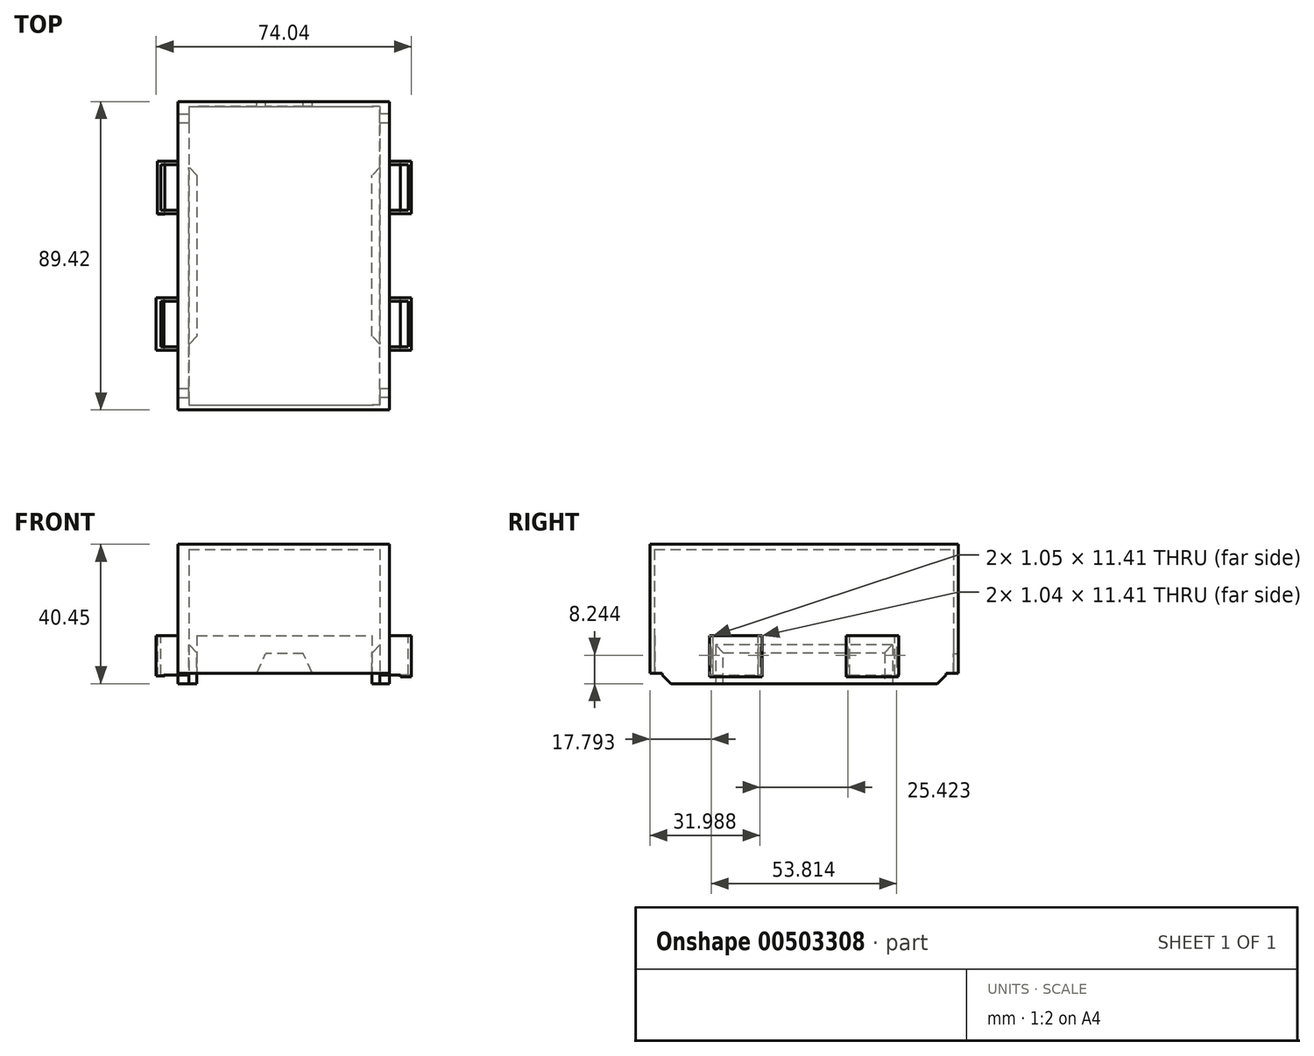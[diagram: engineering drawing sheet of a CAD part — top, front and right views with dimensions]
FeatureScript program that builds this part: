
annotation { "Feature Type Name" : "Feature", "Feature Type Description" : "" }
export const myFeature = defineFeature(function(context is Context, id is Id, definition is map)
    precondition{}
    {
        {
            var Q0;
            Q0=qCreatedBy(makeId("Top.planeOp"),FACE);
            var sketch = newSketch(context, id + "F0", { "sketchPlane" : qUnion([Q0])});
            skLineSegment(sketch, "E0.bottom", {"start": v(-30.48, 45.72) * mm, "end": v(30.48, 45.72) * mm});
            skLineSegment(sketch, "E0.top", {"start": v(-30.48, -45.72) * mm, "end": v(30.48, -45.72) * mm});
            skLineSegment(sketch, "E0.left", {"start": v(-30.48, 45.72) * mm, "end": v(-30.48, -45.72) * mm});
            skLineSegment(sketch, "E0.right", {"start": v(30.48, 45.72) * mm, "end": v(30.48, -45.72) * mm});
            skPoint(sketch, "E0.middle", {"position": v(0, 0) * mm});
            skLineSegment(sketch, "E1.bottom", {"start": v(-25.4, 43.3) * mm, "end": v(25.4, 43.3) * mm});
            skLineSegment(sketch, "E1.top", {"start": v(-25.4, -43.3) * mm, "end": v(25.4, -43.3) * mm});
            skLineSegment(sketch, "E1.left", {"start": v(-25.4, 43.3) * mm, "end": v(-25.4, -43.3) * mm});
            skLineSegment(sketch, "E1.right", {"start": v(25.4, 43.3) * mm, "end": v(25.4, -43.3) * mm});
            skSolve(sketch);
        }
        {
            var Q0;
            Q0=makeQuery(id+"F0.imprint","IMPRINT",FACE,{"disambiguationData":[TD([[makeQuery(id+"F0.imprint","IMPRINT",EDGE,{"derivedFrom":sQuery(id+"F0.wireOp",EDGE,"E0.bottom")}),-1.0]])]});
            extrude(context, id + "F1", {"entities" : qUnion([Q0]), "depth" : 28.45 * mm});
        }
        {
            var Q0;
            Q0=makeQuery(id+"F1.opExtrude","SWEPT_FACE",FACE,{"disambiguationData":[OSD([sQuery(id+"F0.wireOp",EDGE,"E0.bottom")])]});
            var sketch = newSketch(context, id + "F2", { "sketchPlane" : qUnion([Q0])});
            skLineSegment(sketch, "E2", {"start": v(30.48, 14.22) * mm, "end": v(-30.48, 14.22) * mm, "construction": true});
            skPoint(sketch, "E3.middle", {"position": v(0, 28.45) * mm});
            skLineSegment(sketch, "E4", {"start": v(0, 0) * mm, "end": v(-9.48, 0) * mm});
            skLineSegment(sketch, "E5.bottom", {"start": v(-5.46, 19.69) * mm, "end": v(5.46, 19.69) * mm});
            skLineSegment(sketch, "E5.top", {"start": v(-5.46, 8.76) * mm, "end": v(5.46, 8.76) * mm});
            skPoint(sketch, "E5.middle", {"position": v(0, 14.22) * mm});
            skLineSegment(sketch, "E6", {"start": v(-9.48, 0) * mm, "end": v(-5.46, 8.76) * mm});
            skLineSegment(sketch, "E7.MirrorCS", {"start": v(0, 0) * mm, "end": v(9.48, 0) * mm});
            skLineSegment(sketch, "E8.MirrorCS", {"start": v(9.48, 0) * mm, "end": v(5.46, 8.76) * mm});
            skLineSegment(sketch, "E9.MirrorCS", {"start": v(-5.46, 19.68) * mm, "end": v(5.46, 19.68) * mm});
            skLineSegment(sketch, "E10.MirrorCS", {"start": v(-9.48, 28.45) * mm, "end": v(-5.46, 19.68) * mm});
            skLineSegment(sketch, "E11.MirrorCS", {"start": v(0, 28.45) * mm, "end": v(-9.48, 28.45) * mm});
            skLineSegment(sketch, "E12.MirrorCS", {"start": v(0, 28.45) * mm, "end": v(9.48, 28.45) * mm});
            skLineSegment(sketch, "E13.MirrorCS", {"start": v(9.48, 28.45) * mm, "end": v(5.46, 19.68) * mm});
            skSolve(sketch);
        }
        {
            var Q0;
            Q0=qSketchRegion(id+"F2",true);
            var Q1;
            {var subQ1=sQuery(id+"F2.wireOp",EDGE,"z2dX2tQm-mAHQ-A0xj-hADe-n06FKAJlfdiZ.bottom");Q1=makeQuery(id+"F2.imprint","IMPRINT",FACE,{"disambiguationData":[TD([[makeQuery(id+"F2.imprint","IMPRINT",EDGE,{"derivedFrom":subQ1}),-1.0]])]});}
            extrude(context, id + "F3", {"entities" : qUnion([Q0, Q1]), "operationType" : NewBodyOperationType.REMOVE, "oppositeDirection" : true, "depth" : 25.4 * mm});
        }
        {
            var Q0;
            Q0=qCreatedBy(makeId("Top.planeOp"),FACE);
            var sketch = newSketch(context, id + "F4", { "sketchPlane" : qUnion([Q0])});
            skLineSegment(sketch, "E14.bottom", {"start": v(33.22, 48.14) * mm, "end": v(-33.43, 48.14) * mm});
            skLineSegment(sketch, "E14.top", {"start": v(33.22, 41.15) * mm, "end": v(-33.43, 41.15) * mm});
            skLineSegment(sketch, "E14.left", {"start": v(33.22, 48.14) * mm, "end": v(33.22, 41.15) * mm});
            skLineSegment(sketch, "E14.right", {"start": v(-33.43, 48.14) * mm, "end": v(-33.43, 41.15) * mm});
            skLineSegment(sketch, "E15.MirrorCS", {"start": v(33.22, -41.15) * mm, "end": v(-33.43, -41.15) * mm});
            skLineSegment(sketch, "E16.MirrorCS", {"start": v(33.22, -48.14) * mm, "end": v(33.22, -41.15) * mm});
            skLineSegment(sketch, "E17.MirrorCS", {"start": v(-33.43, -48.14) * mm, "end": v(-33.43, -41.15) * mm});
            skLineSegment(sketch, "E18.MirrorCS", {"start": v(33.22, -48.14) * mm, "end": v(-33.43, -48.14) * mm});
            skSolve(sketch);
        }
        {
            var Q0;
            Q0=qSketchRegion(id+"F4",true);
            extrude(context, id + "F5", {"entities" : qUnion([Q0]), "operationType" : NewBodyOperationType.REMOVE, "depth" : 3.05 * mm});
        }
        {
            var Q0;
            Q0=makeQuery(id+"F1.opExtrude","CAP_FACE",FACE,{"disambiguationData":[OSD([sQuery(id+"F0.wireOp",EDGE,"E0.bottom"),sQuery(id+"F0.wireOp",EDGE,"E0.top"),sQuery(id+"F0.wireOp",EDGE,"E0.left"),sQuery(id+"F0.wireOp",EDGE,"E0.right"),sQuery(id+"F0.wireOp",EDGE,"E1.bottom"),sQuery(id+"F0.wireOp",EDGE,"E1.top"),sQuery(id+"F0.wireOp",EDGE,"E1.left"),sQuery(id+"F0.wireOp",EDGE,"E1.right")])],"isStart":false});
            var sketch = newSketch(context, id + "F6", { "sketchPlane" : qUnion([Q0])});
            skLineSegment(sketch, "E19.bottom", {"start": v(30.48, 45.72) * mm, "end": v(-34.49, 45.72) * mm});
            skLineSegment(sketch, "E19.top", {"start": v(30.48, 40.94) * mm, "end": v(-34.49, 40.94) * mm});
            skLineSegment(sketch, "E19.left", {"start": v(30.48, 45.72) * mm, "end": v(30.48, 40.94) * mm});
            skLineSegment(sketch, "E19.right", {"start": v(-34.49, 45.72) * mm, "end": v(-34.49, 40.94) * mm});
            skLineSegment(sketch, "E20.MirrorCS", {"start": v(30.48, -40.94) * mm, "end": v(-34.49, -40.94) * mm});
            skLineSegment(sketch, "E21.MirrorCS", {"start": v(30.48, -45.72) * mm, "end": v(30.48, -40.94) * mm});
            skLineSegment(sketch, "E22.MirrorCS", {"start": v(-34.49, -45.72) * mm, "end": v(-34.49, -40.94) * mm});
            skLineSegment(sketch, "E23.MirrorCS", {"start": v(30.48, -45.72) * mm, "end": v(-34.49, -45.72) * mm});
            skSolve(sketch);
        }
        {
            var Q0;
            Q0=qSketchRegion(id+"F6",true);
            extrude(context, id + "F7", {"entities" : qUnion([Q0]), "operationType" : NewBodyOperationType.REMOVE, "oppositeDirection" : true, "depth" : 3.05 * mm});
        }
        {
            var Q0;
            Q0=makeQuery(id+"F1.opExtrude","SWEPT_FACE",FACE,{"disambiguationData":[OSD([sQuery(id+"F0.wireOp",EDGE,"E1.right")])]});
            var sketch = newSketch(context, id + "F8", { "sketchPlane" : qUnion([Q0])});
            skLineSegment(sketch, "E24.bottom", {"start": v(-41.15, 0) * mm, "end": v(-25.91, 0) * mm});
            skLineSegment(sketch, "E24.top", {"start": v(-41.15, 30.48) * mm, "end": v(-25.91, 30.48) * mm});
            skLineSegment(sketch, "E24.right", {"start": v(-25.91, 0) * mm, "end": v(-25.91, 30.48) * mm});
            skLineSegment(sketch, "E25", {"start": v(0, 0) * mm, "end": v(0, 28.45) * mm, "construction": true});
            skLineSegment(sketch, "E26.MirrorCS", {"start": v(25.91, 0) * mm, "end": v(25.91, 30.48) * mm});
            skLineSegment(sketch, "E27.MirrorCS", {"start": v(41.15, 30.48) * mm, "end": v(25.91, 30.48) * mm});
            skLineSegment(sketch, "E28.MirrorCS", {"start": v(41.15, 0) * mm, "end": v(25.91, 0) * mm});
            skLineSegment(sketch, "E29", {"start": v(-41.15, 30.48) * mm, "end": v(-43.09, 30.48) * mm});
            skLineSegment(sketch, "E30", {"start": v(-43.09, 30.48) * mm, "end": v(-43.09, 0) * mm});
            skLineSegment(sketch, "E31", {"start": v(-43.09, 0) * mm, "end": v(-41.15, 0) * mm});
            skLineSegment(sketch, "E32.MirrorCS", {"start": v(41.15, 30.48) * mm, "end": v(43.09, 30.48) * mm});
            skLineSegment(sketch, "E33.MirrorCS", {"start": v(43.09, 30.48) * mm, "end": v(43.09, 0) * mm});
            skLineSegment(sketch, "E34.MirrorCS", {"start": v(43.09, 0) * mm, "end": v(41.15, 0) * mm});
            skSolve(sketch);
        }
        {
            var Q0;
            Q0=qSketchRegion(id+"F8",true);
            extrude(context, id + "F9", {"entities" : qUnion([Q0]), "operationType" : NewBodyOperationType.REMOVE, "oppositeDirection" : true, "depth" : 2.3 * mm});
        }
        {
            var Q0;
            Q0=qCreatedBy(makeId("Right.planeOp"),FACE);
            var sketch = newSketch(context, id + "F10", { "sketchPlane" : qUnion([Q0])});
            skLineSegment(sketch, "E35.bottom", {"start": v(51.68, -10.67) * mm, "end": v(-48.17, -10.67) * mm});
            skLineSegment(sketch, "E35.top", {"start": v(51.68, 37.54) * mm, "end": v(-48.17, 37.54) * mm});
            skLineSegment(sketch, "E35.left", {"start": v(51.68, -10.67) * mm, "end": v(51.68, 37.54) * mm});
            skLineSegment(sketch, "E35.right", {"start": v(-48.17, -10.67) * mm, "end": v(-48.17, 37.54) * mm});
            skSolve(sketch);
        }
        {
            var Q0;
            Q0=qSketchRegion(id+"F10",true);
            extrude(context, id + "F11", {"entities" : qUnion([Q0]), "operationType" : NewBodyOperationType.REMOVE, "oppositeDirection" : true, "depth" : 50.8 * mm});
        }
        {
            var Q0;
            Q0=makeQuery(id+"F1.opExtrude","SWEPT_BODY",BODY,{"disambiguationData":[OSD([sQuery(id+"F0.wireOp",EDGE,"E0.bottom"),sQuery(id+"F0.wireOp",EDGE,"E0.top"),sQuery(id+"F0.wireOp",EDGE,"E0.left"),sQuery(id+"F0.wireOp",EDGE,"E0.right"),sQuery(id+"F0.wireOp",EDGE,"E1.bottom"),sQuery(id+"F0.wireOp",EDGE,"E1.top"),sQuery(id+"F0.wireOp",EDGE,"E1.left"),sQuery(id+"F0.wireOp",EDGE,"E1.right")])]});
            var Q1;
            Q1=qCreatedBy(makeId("Right.planeOp"),FACE);
            mirror(context, id + "F12", {"operationType" : NewBodyOperationType.ADD, "entities" : qUnion([Q0]), "mirrorPlane" : qUnion([Q1])});
        }
        {
            var Q0;
            {var subQ1=sQuery(id+"F0.wireOp",EDGE,"E0.right");var subQ2=sQuery(id+"F6.wireOp",EDGE,"E19.top");Q0=makeQuery(id+"F12.opPattern","COPY",EDGE,{"derivedFrom":makeQuery(id+"F7.boolean.opBoolean","COPY",EDGE,{"disambiguationData":[TD([makeQuery(id+"F1.opExtrude","SWEPT_FACE",FACE,{"disambiguationData":[OSD([subQ1])]})])],"derivedFrom":makeQuery(id+"F7.opExtrude","CAP_EDGE",EDGE,{"disambiguationData":[OSD([subQ2])],"isStart":true})}),"instanceName":"1"});}
            var Q1;
            {var subQ1=sQuery(id+"F0.wireOp",EDGE,"E0.right");var subQ2=sQuery(id+"F4.wireOp",EDGE,"E14.top");Q1=makeQuery(id+"F12.opPattern","COPY",EDGE,{"derivedFrom":makeQuery(id+"F5.boolean.opBoolean","COPY",EDGE,{"disambiguationData":[TD([makeQuery(id+"F1.opExtrude","SWEPT_FACE",FACE,{"disambiguationData":[OSD([subQ1])]})])],"derivedFrom":makeQuery(id+"F5.opExtrude","CAP_EDGE",EDGE,{"disambiguationData":[OSD([subQ2])],"isStart":true})}),"instanceName":"1"});}
            var Q2;
            {var subQ1=sQuery(id+"F0.wireOp",EDGE,"E0.right");var subQ2=sQuery(id+"F6.wireOp",EDGE,"E19.top");Q2=makeQuery(id+"F7.boolean.opBoolean","COPY",EDGE,{"disambiguationData":[TD([makeQuery(id+"F1.opExtrude","SWEPT_FACE",FACE,{"disambiguationData":[OSD([subQ1])]})])],"derivedFrom":makeQuery(id+"F7.opExtrude","CAP_EDGE",EDGE,{"disambiguationData":[OSD([subQ2])],"isStart":true})});}
            var Q3;
            {var subQ1=sQuery(id+"F0.wireOp",EDGE,"E0.right");var subQ2=sQuery(id+"F6.wireOp",EDGE,"E20.MirrorCS");Q3=makeQuery(id+"F7.boolean.opBoolean","COPY",EDGE,{"disambiguationData":[TD([makeQuery(id+"F1.opExtrude","SWEPT_FACE",FACE,{"disambiguationData":[OSD([subQ1])]})])],"derivedFrom":makeQuery(id+"F7.opExtrude","CAP_EDGE",EDGE,{"disambiguationData":[OSD([subQ2])],"isStart":true})});}
            var Q4;
            {var subQ1=sQuery(id+"F0.wireOp",EDGE,"E0.right");var subQ2=sQuery(id+"F6.wireOp",EDGE,"E20.MirrorCS");Q4=makeQuery(id+"F12.opPattern","COPY",EDGE,{"derivedFrom":makeQuery(id+"F7.boolean.opBoolean","COPY",EDGE,{"disambiguationData":[TD([makeQuery(id+"F1.opExtrude","SWEPT_FACE",FACE,{"disambiguationData":[OSD([subQ1])]})])],"derivedFrom":makeQuery(id+"F7.opExtrude","CAP_EDGE",EDGE,{"disambiguationData":[OSD([subQ2])],"isStart":true})}),"instanceName":"1"});}
            var Q5;
            {var subQ1=sQuery(id+"F0.wireOp",EDGE,"E0.right");var subQ2=sQuery(id+"F4.wireOp",EDGE,"E15.MirrorCS");Q5=makeQuery(id+"F12.opPattern","COPY",EDGE,{"derivedFrom":makeQuery(id+"F5.boolean.opBoolean","COPY",EDGE,{"disambiguationData":[TD([makeQuery(id+"F1.opExtrude","SWEPT_FACE",FACE,{"disambiguationData":[OSD([subQ1])]})])],"derivedFrom":makeQuery(id+"F5.opExtrude","CAP_EDGE",EDGE,{"disambiguationData":[OSD([subQ2])],"isStart":true})}),"instanceName":"1"});}
            var Q6;
            {var subQ1=sQuery(id+"F0.wireOp",EDGE,"E0.right");var subQ2=sQuery(id+"F4.wireOp",EDGE,"E15.MirrorCS");Q6=makeQuery(id+"F5.boolean.opBoolean","COPY",EDGE,{"disambiguationData":[TD([makeQuery(id+"F1.opExtrude","SWEPT_FACE",FACE,{"disambiguationData":[OSD([subQ1])]})])],"derivedFrom":makeQuery(id+"F5.opExtrude","CAP_EDGE",EDGE,{"disambiguationData":[OSD([subQ2])],"isStart":true})});}
            var Q7;
            {var subQ1=sQuery(id+"F0.wireOp",EDGE,"E0.right");var subQ2=sQuery(id+"F4.wireOp",EDGE,"E14.top");Q7=makeQuery(id+"F5.boolean.opBoolean","COPY",EDGE,{"disambiguationData":[TD([makeQuery(id+"F1.opExtrude","SWEPT_FACE",FACE,{"disambiguationData":[OSD([subQ1])]})])],"derivedFrom":makeQuery(id+"F5.opExtrude","CAP_EDGE",EDGE,{"disambiguationData":[OSD([subQ2])],"isStart":true})});}
            var Q8;
            Q8=makeQuery(id+"F9.boolean.opBoolean","COPY",EDGE,{"derivedFrom":makeQuery(id+"F9.opExtrude","CAP_EDGE",EDGE,{"disambiguationData":[OSD([sQuery(id+"F8.wireOp",EDGE,"E24.right")])],"isStart":true})});
            var Q9;
            Q9=makeQuery(id+"F9.boolean.opBoolean","COPY",EDGE,{"derivedFrom":makeQuery(id+"F9.opExtrude","CAP_EDGE",EDGE,{"disambiguationData":[OSD([sQuery(id+"F8.wireOp",EDGE,"E26.MirrorCS")])],"isStart":true})});
            var Q10;
            Q10=makeQuery(id+"F12.opPattern","COPY",EDGE,{"derivedFrom":makeQuery(id+"F9.boolean.opBoolean","COPY",EDGE,{"derivedFrom":makeQuery(id+"F9.opExtrude","CAP_EDGE",EDGE,{"disambiguationData":[OSD([sQuery(id+"F8.wireOp",EDGE,"E24.right")])],"isStart":true})}),"instanceName":"1"});
            var Q11;
            Q11=makeQuery(id+"F12.opPattern","COPY",EDGE,{"derivedFrom":makeQuery(id+"F9.boolean.opBoolean","COPY",EDGE,{"derivedFrom":makeQuery(id+"F9.opExtrude","CAP_EDGE",EDGE,{"disambiguationData":[OSD([sQuery(id+"F8.wireOp",EDGE,"E26.MirrorCS")])],"isStart":true})}),"instanceName":"1"});
            chamfer(context, id + "F13", {"entities" : qUnion([Q0, Q1, Q2, Q3, Q4, Q5, Q6, Q7, Q8, Q9, Q10, Q11]), "width" : 2.54 * mm, "tangentPropagation" : true});
        }
        {
            var Q0;
            Q0=makeQuery(id+"F1.opExtrude","SWEPT_FACE",FACE,{"disambiguationData":[OSD([sQuery(id+"F0.wireOp",EDGE,"E0.right")])]});
            var sketch = newSketch(context, id + "F14", { "sketchPlane" : qUnion([Q0])});
            skLineSegment(sketch, "E36.bottom", {"start": v(-27.43, 25.9) * mm, "end": v(-12.2, 25.9) * mm});
            skLineSegment(sketch, "E36.top", {"start": v(-27.43, 2.54) * mm, "end": v(-12.2, 2.54) * mm});
            skLineSegment(sketch, "E36.left", {"start": v(-27.43, 25.9) * mm, "end": v(-27.43, 2.54) * mm});
            skLineSegment(sketch, "E36.right", {"start": v(-12.2, 25.9) * mm, "end": v(-12.2, 2.54) * mm});
            skLineSegment(sketch, "E37.MirrorCS", {"start": v(12.2, 25.9) * mm, "end": v(12.2, 2.54) * mm});
            skLineSegment(sketch, "E38.MirrorCS", {"start": v(27.43, 25.9) * mm, "end": v(12.2, 25.9) * mm});
            skLineSegment(sketch, "E39.MirrorCS", {"start": v(27.43, 2.54) * mm, "end": v(12.2, 2.54) * mm});
            skLineSegment(sketch, "E40.MirrorCS", {"start": v(27.43, 25.9) * mm, "end": v(27.43, 2.54) * mm});
            skSolve(sketch);
        }
        {
            var Q0;
            Q0=qSketchRegion(id+"F14",true);
            extrude(context, id + "F15", {"entities" : qUnion([Q0]), "operationType" : NewBodyOperationType.ADD, "depth" : 6.35 * mm});
        }
        {
            var Q0;
            Q0=makeQuery(id+"F15.opExtrude","SWEPT_FACE",FACE,{"disambiguationData":[OSD([sQuery(id+"F14.wireOp",EDGE,"E36.bottom")])]});
            var sketch = newSketch(context, id + "F16", { "sketchPlane" : qUnion([Q0])});
            skLineSegment(sketch, "E41.bottom", {"start": v(30.48, -26.38) * mm, "end": v(35.84, -26.38) * mm});
            skLineSegment(sketch, "E41.top", {"start": v(30.48, -13.23) * mm, "end": v(35.84, -13.23) * mm});
            skLineSegment(sketch, "E41.left", {"start": v(30.48, -26.38) * mm, "end": v(30.48, -13.23) * mm});
            skLineSegment(sketch, "E41.right", {"start": v(35.84, -26.38) * mm, "end": v(35.84, -13.23) * mm});
            skLineSegment(sketch, "E42.MirrorCS", {"start": v(30.48, 13.23) * mm, "end": v(35.84, 13.23) * mm});
            skLineSegment(sketch, "E43.MirrorCS", {"start": v(35.84, 26.38) * mm, "end": v(35.84, 13.23) * mm});
            skLineSegment(sketch, "E44.MirrorCS", {"start": v(30.48, 26.38) * mm, "end": v(35.84, 26.38) * mm});
            skLineSegment(sketch, "E45.MirrorCS", {"start": v(30.48, 26.38) * mm, "end": v(30.48, 13.23) * mm});
            skSolve(sketch);
        }
        {
            var Q0;
            Q0=qSketchRegion(id+"F16",true);
            extrude(context, id + "F17", {"entities" : qUnion([Q0]), "operationType" : NewBodyOperationType.REMOVE, "endBound" : BoundingType.THROUGH_ALL, "oppositeDirection" : true, "depth" : 25.4 * mm});
        }
        {
            var Q0;
            Q0=makeQuery(id+"F1.opExtrude","SWEPT_BODY",BODY,{"disambiguationData":[OSD([sQuery(id+"F0.wireOp",EDGE,"E0.bottom"),sQuery(id+"F0.wireOp",EDGE,"E0.top"),sQuery(id+"F0.wireOp",EDGE,"E0.left"),sQuery(id+"F0.wireOp",EDGE,"E0.right"),sQuery(id+"F0.wireOp",EDGE,"E1.bottom"),sQuery(id+"F0.wireOp",EDGE,"E1.top"),sQuery(id+"F0.wireOp",EDGE,"E1.left"),sQuery(id+"F0.wireOp",EDGE,"E1.right")])]});
            var Q1;
            Q1=qCreatedBy(makeId("Right.planeOp"),FACE);
            mirror(context, id + "F18", {"operationType" : NewBodyOperationType.ADD, "entities" : qUnion([Q0]), "mirrorPlane" : qUnion([Q1])});
        }
        {
            var Q0;
            Q0=makeQuery(id+"F9.boolean.opBoolean","COPY",FACE,{"derivedFrom":makeQuery(id+"F9.opExtrude","SWEPT_FACE",FACE,{"disambiguationData":[OSD([sQuery(id+"F8.wireOp",EDGE,"E33.MirrorCS")])]})});
            var Q1;
            Q1=makeQuery(id+"F12.opPattern","COPY",FACE,{"derivedFrom":makeQuery(id+"F9.boolean.opBoolean","COPY",FACE,{"derivedFrom":makeQuery(id+"F9.opExtrude","SWEPT_FACE",FACE,{"disambiguationData":[OSD([sQuery(id+"F8.wireOp",EDGE,"E33.MirrorCS")])]})}),"instanceName":"1"});
            extrude(context, id + "F19", {"entities" : qUnion([Q0, Q1]), "operationType" : NewBodyOperationType.REMOVE, "oppositeDirection" : true, "depth" : 0.25 * mm});
        }
        {
            var Q0;
            Q0=makeQuery(id+"F9.boolean.opBoolean","COPY",FACE,{"derivedFrom":makeQuery(id+"F9.opExtrude","SWEPT_FACE",FACE,{"disambiguationData":[OSD([sQuery(id+"F8.wireOp",EDGE,"E30")])]})});
            var Q1;
            Q1=makeQuery(id+"F12.opPattern","COPY",FACE,{"derivedFrom":makeQuery(id+"F9.boolean.opBoolean","COPY",FACE,{"derivedFrom":makeQuery(id+"F9.opExtrude","SWEPT_FACE",FACE,{"disambiguationData":[OSD([sQuery(id+"F8.wireOp",EDGE,"E30")])]})}),"instanceName":"1"});
            extrude(context, id + "F20", {"entities" : qUnion([Q0, Q1]), "operationType" : NewBodyOperationType.REMOVE, "oppositeDirection" : true, "depth" : 0.25 * mm});
        }
        {
            var Q0;
            {var subQ0=makeQuery(id+"F1.opExtrude","SWEPT_FACE",FACE,{"disambiguationData":[OSD([sQuery(id+"F0.wireOp",EDGE,"E0.top")])]});Q0=makeQuery(id+"F12.boolean.opBoolean","MERGE",FACE,{"derivedFrom":[subQ0,makeQuery(id+"F12.opPattern","COPY",FACE,{"derivedFrom":subQ0,"instanceName":"1"})]});}
            extrude(context, id + "F21", {"entities" : qUnion([Q0]), "operationType" : NewBodyOperationType.REMOVE, "oppositeDirection" : true, "depth" : 1.02 * mm});
        }
        {
            var Q0;
            Q0=makeQuery(id+"F18.opPattern","COPY",FACE,{"derivedFrom":makeQuery(id+"F15.opExtrude","SWEPT_FACE",FACE,{"disambiguationData":[OSD([sQuery(id+"F14.wireOp",EDGE,"E38.MirrorCS")])]}),"instanceName":"1"});
            var sketch = newSketch(context, id + "F22", { "sketchPlane" : qUnion([Q0])});
            skLineSegment(sketch, "E46.bottom", {"start": v(-36.83, 27.43) * mm, "end": v(-33.66, 27.43) * mm});
            skLineSegment(sketch, "E46.top", {"start": v(-36.83, 12.2) * mm, "end": v(-33.66, 12.2) * mm});
            skLineSegment(sketch, "E46.left", {"start": v(-36.83, 27.43) * mm, "end": v(-36.83, 12.2) * mm});
            skLineSegment(sketch, "E46.right", {"start": v(-33.66, 27.43) * mm, "end": v(-33.66, 12.2) * mm});
            skLineSegment(sketch, "E47.bottom", {"start": v(-33.66, -12.01) * mm, "end": v(-36.83, -12.01) * mm});
            skLineSegment(sketch, "E47.top", {"start": v(-33.66, -27.44) * mm, "end": v(-36.83, -27.44) * mm});
            skLineSegment(sketch, "E47.left", {"start": v(-33.66, -12.01) * mm, "end": v(-33.66, -27.44) * mm});
            skLineSegment(sketch, "E47.right", {"start": v(-36.83, -12.01) * mm, "end": v(-36.83, -27.44) * mm});
            skSolve(sketch);
        }
        {
            var Q0;
            Q0=qSketchRegion(id+"F22",true);
            extrude(context, id + "F23", {"entities" : qUnion([Q0]), "operationType" : NewBodyOperationType.ADD, "depth" : 0.5 * mm});
        }
        {
            var Q0;
            Q0=makeQuery(id+"F15.opExtrude","SWEPT_FACE",FACE,{"disambiguationData":[OSD([sQuery(id+"F14.wireOp",EDGE,"E36.top")])]});
            var sketch = newSketch(context, id + "F24", { "sketchPlane" : qUnion([Q0])});
            skLineSegment(sketch, "E48.bottom", {"start": v(36.83, 27.43) * mm, "end": v(33.66, 27.43) * mm});
            skLineSegment(sketch, "E48.top", {"start": v(36.83, 12.2) * mm, "end": v(33.66, 12.2) * mm});
            skLineSegment(sketch, "E48.left", {"start": v(36.83, 27.43) * mm, "end": v(36.83, 12.2) * mm});
            skLineSegment(sketch, "E48.right", {"start": v(33.66, 27.43) * mm, "end": v(33.66, 12.2) * mm});
            skLineSegment(sketch, "E49.bottom", {"start": v(36.83, -12.2) * mm, "end": v(33.66, -12.2) * mm});
            skLineSegment(sketch, "E49.top", {"start": v(36.83, -27.38) * mm, "end": v(33.66, -27.38) * mm});
            skLineSegment(sketch, "E49.left", {"start": v(36.83, -12.2) * mm, "end": v(36.83, -27.38) * mm});
            skLineSegment(sketch, "E49.right", {"start": v(33.66, -12.2) * mm, "end": v(33.66, -27.38) * mm});
            skSolve(sketch);
        }
        {
            var Q0;
            Q0=qSketchRegion(id+"F24",true);
            extrude(context, id + "F25", {"entities" : qUnion([Q0]), "operationType" : NewBodyOperationType.ADD, "depth" : 0.5 * mm});
        }
        {
            var Q0;
            Q0=makeQuery(id+"F15.opExtrude","SWEPT_FACE",FACE,{"disambiguationData":[OSD([sQuery(id+"F14.wireOp",EDGE,"E36.bottom")])]});
            var sketch = newSketch(context, id + "F26", { "sketchPlane" : qUnion([Q0])});
            skLineSegment(sketch, "E50.bottom", {"start": v(36.83, -27.43) * mm, "end": v(35.34, -27.43) * mm});
            skLineSegment(sketch, "E50.top", {"start": v(36.83, -12.2) * mm, "end": v(35.34, -12.2) * mm});
            skLineSegment(sketch, "E50.left", {"start": v(36.83, -27.43) * mm, "end": v(36.83, -12.2) * mm});
            skLineSegment(sketch, "E50.right", {"start": v(35.34, -27.43) * mm, "end": v(35.34, -12.2) * mm});
            skLineSegment(sketch, "E51.bottom", {"start": v(35.34, 12.22) * mm, "end": v(36.83, 12.22) * mm});
            skLineSegment(sketch, "E51.top", {"start": v(35.34, 27.38) * mm, "end": v(36.83, 27.38) * mm});
            skLineSegment(sketch, "E51.left", {"start": v(35.34, 12.22) * mm, "end": v(35.34, 27.38) * mm});
            skLineSegment(sketch, "E51.right", {"start": v(36.83, 12.22) * mm, "end": v(36.83, 27.38) * mm});
            skSolve(sketch);
        }
        {
            var Q0;
            Q0=qSketchRegion(id+"F26",true);
            extrude(context, id + "F27", {"entities" : qUnion([Q0]), "operationType" : NewBodyOperationType.ADD, "depth" : 0.5 * mm});
        }
        {
            var Q0;
            Q0=makeQuery(id+"F18.opPattern","COPY",FACE,{"derivedFrom":makeQuery(id+"F15.opExtrude","SWEPT_FACE",FACE,{"disambiguationData":[OSD([sQuery(id+"F14.wireOp",EDGE,"E36.top")])]}),"instanceName":"1"});
            var sketch = newSketch(context, id + "F28", { "sketchPlane" : qUnion([Q0])});
            skLineSegment(sketch, "E52.bottom", {"start": v(-36.83, 12.2) * mm, "end": v(-35.32, 12.2) * mm});
            skLineSegment(sketch, "E52.top", {"start": v(-36.83, 27.43) * mm, "end": v(-35.32, 27.43) * mm});
            skLineSegment(sketch, "E52.left", {"start": v(-36.83, 12.2) * mm, "end": v(-36.83, 27.43) * mm});
            skLineSegment(sketch, "E52.right", {"start": v(-35.32, 12.2) * mm, "end": v(-35.32, 27.43) * mm});
            skLineSegment(sketch, "E53.bottom", {"start": v(-36.83, -12.06) * mm, "end": v(-35.34, -12.06) * mm});
            skLineSegment(sketch, "E53.top", {"start": v(-36.83, -27.45) * mm, "end": v(-35.34, -27.45) * mm});
            skLineSegment(sketch, "E53.left", {"start": v(-36.83, -12.06) * mm, "end": v(-36.83, -27.45) * mm});
            skLineSegment(sketch, "E53.right", {"start": v(-35.34, -12.06) * mm, "end": v(-35.34, -27.45) * mm});
            skSolve(sketch);
        }
        {
            var Q0;
            Q0=qSketchRegion(id+"F28",true);
            extrude(context, id + "F29", {"entities" : qUnion([Q0]), "operationType" : NewBodyOperationType.ADD, "depth" : 0.25 * mm});
        }
        {
            var Q0;
            Q0=makeQuery(id+"F12.opPattern","COPY",FACE,{"derivedFrom":makeQuery(id+"F1.opExtrude","SWEPT_FACE",FACE,{"disambiguationData":[OSD([sQuery(id+"F0.wireOp",EDGE,"E0.right")])]}),"instanceName":"1"});
            var Q1;
            Q1=makeQuery(id+"F29.opExtrude","SWEPT_FACE",FACE,{"disambiguationData":[OSD([sQuery(id+"F28.wireOp",EDGE,"E52.right")])]});
            var Q2;
            Q2=makeQuery(id+"F18.opPattern","COPY",FACE,{"derivedFrom":makeQuery(id+"F17.boolean.opBoolean","COPY",FACE,{"derivedFrom":makeQuery(id+"F17.opExtrude","SWEPT_FACE",FACE,{"disambiguationData":[OSD([sQuery(id+"F16.wireOp",EDGE,"E41.right")])]})}),"instanceName":"1"});
            var Q3;
            Q3=makeQuery(id+"F29.boolean.opBoolean","MERGE",FACE,{"derivedFrom":[makeQuery(id+"F23.boolean.opBoolean","MERGE",FACE,{"derivedFrom":[makeQuery(id+"F18.opPattern","COPY",FACE,{"derivedFrom":makeQuery(id+"F15.opExtrude","CAP_FACE",FACE,{"disambiguationData":[OSD([sQuery(id+"F14.wireOp",EDGE,"E36.bottom"),sQuery(id+"F14.wireOp",EDGE,"E36.top"),sQuery(id+"F14.wireOp",EDGE,"E36.left"),sQuery(id+"F14.wireOp",EDGE,"E36.right")])],"isStart":false}),"instanceName":"1"}),makeQuery(id+"F23.opExtrude","SWEPT_FACE",FACE,{"disambiguationData":[OSD([sQuery(id+"F22.wireOp",EDGE,"E47.right")])]})]}),makeQuery(id+"F29.opExtrude","SWEPT_FACE",FACE,{"disambiguationData":[OSD([sQuery(id+"F28.wireOp",EDGE,"E52.left")])]})]});
            extrude(context, id + "F30", {"entities" : qUnion([Q0, Q1, Q2, Q3]), "operationType" : NewBodyOperationType.ADD, "depth" : 0.38 * mm});
        }
        {
            var Q0;
            Q0=makeQuery(id+"F29.opExtrude","SWEPT_FACE",FACE,{"disambiguationData":[OSD([sQuery(id+"F28.wireOp",EDGE,"E53.right")])]});
            extrude(context, id + "F31", {"entities" : qUnion([Q0]), "operationType" : NewBodyOperationType.ADD, "depth" : 0.25 * mm});
        }
        {
            var Q0;
            {var subQ0=sQuery(id+"F0.wireOp",EDGE,"E0.right");var subQ1=sQuery(id+"F0.wireOp",EDGE,"E1.right");Q0=makeQuery(id+"F7.boolean.opBoolean","SPLIT",FACE,{"disambiguationData":[TD([makeQuery(id+"F1.opExtrude","SWEPT_FACE",FACE,{"disambiguationData":[OSD([subQ0])]})])],"derivedFrom":makeQuery(id+"F1.opExtrude","CAP_FACE",FACE,{"disambiguationData":[OSD([sQuery(id+"F0.wireOp",EDGE,"E0.bottom"),sQuery(id+"F0.wireOp",EDGE,"E0.top"),sQuery(id+"F0.wireOp",EDGE,"E0.left"),subQ0,sQuery(id+"F0.wireOp",EDGE,"E1.bottom"),sQuery(id+"F0.wireOp",EDGE,"E1.top"),sQuery(id+"F0.wireOp",EDGE,"E1.left"),subQ1])],"isStart":false})});}
            var sketch = newSketch(context, id + "F32", { "sketchPlane" : qUnion([Q0])});
            skLineSegment(sketch, "E54.bottom", {"start": v(64.06, -66.08) * mm, "end": v(-41.9, -66.08) * mm});
            skLineSegment(sketch, "E54.top", {"start": v(64.06, 50.2) * mm, "end": v(-41.9, 50.2) * mm});
            skLineSegment(sketch, "E54.left", {"start": v(64.06, -66.08) * mm, "end": v(64.06, 50.2) * mm});
            skLineSegment(sketch, "E54.right", {"start": v(-41.9, -66.08) * mm, "end": v(-41.9, 50.2) * mm});
            skSolve(sketch);
        }
        {
            var Q0;
            Q0 = qSketchRegion(id + "F32", true);
            extrude(context, id + "F33", {"entities" : qUnion([Q0]), "operationType" : NewBodyOperationType.REMOVE, "oppositeDirection" : true, "depth" : 14.5 * mm});
        }
        {
            var Q0;
            Q0=makeQuery(id+"F33.boolean.opBoolean","COPY",FACE,{"derivedFrom":makeQuery(id+"F33.opExtrude","CAP_FACE",FACE,{"disambiguationData":[OSD([sQuery(id+"F32.wireOp",EDGE,"E54.bottom"),sQuery(id+"F32.wireOp",EDGE,"E54.top"),sQuery(id+"F32.wireOp",EDGE,"E54.left"),sQuery(id+"F32.wireOp",EDGE,"E54.right")])],"isStart":false})});
            var sketch = newSketch(context, id + "F34", { "sketchPlane" : qUnion([Q0])});
            skLineSegment(sketch, "E55.bottom", {"start": v(-30.86, -44.7) * mm, "end": v(30.48, -44.7) * mm});
            skLineSegment(sketch, "E55.top", {"start": v(-30.86, 45.72) * mm, "end": v(30.48, 45.72) * mm});
            skLineSegment(sketch, "E55.left", {"start": v(-30.86, -44.7) * mm, "end": v(-30.86, 45.72) * mm});
            skLineSegment(sketch, "E55.right", {"start": v(30.48, -44.7) * mm, "end": v(30.48, 45.72) * mm});
            skLineSegment(sketch, "E56.bottom", {"start": v(-27.69, -43.34) * mm, "end": v(27.69, -43.34) * mm});
            skLineSegment(sketch, "E56.top", {"start": v(-27.69, 43.34) * mm, "end": v(27.69, 43.34) * mm});
            skLineSegment(sketch, "E56.left", {"start": v(-27.69, -43.34) * mm, "end": v(-27.69, 43.34) * mm});
            skLineSegment(sketch, "E56.right", {"start": v(27.69, -43.34) * mm, "end": v(27.69, 43.34) * mm});
            skSolve(sketch);
        }
        {
            var Q0;
            {var subQ27=sQuery(id+"F34.wireOp",EDGE,"E55.top");Q0=makeQuery(id+"F34.imprint","IMPRINT",FACE,{"disambiguationData":[TD([[makeQuery(id+"F34.imprint","IMPRINT",EDGE,{"derivedFrom":subQ27}),-1.0]])]});}
            extrude(context, id + "F35", {"entities" : qUnion([Q0]), "operationType" : NewBodyOperationType.ADD, "depth" : 25 * mm});
        }
        {
            var Q0;
            {var subQ0=sQuery(id+"F0.wireOp",EDGE,"E0.bottom");var subQ1=makeQuery(id+"F1.opExtrude","SWEPT_FACE",FACE,{"disambiguationData":[OSD([subQ0])]});Q0=makeQuery(id+"F35.boolean.opBoolean","MERGE",FACE,{"derivedFrom":[makeQuery(id+"F30.boolean.opBoolean","MERGE",FACE,{"derivedFrom":[makeQuery(id+"F12.boolean.opBoolean","MERGE",FACE,{"derivedFrom":[subQ1,makeQuery(id+"F12.opPattern","COPY",FACE,{"derivedFrom":subQ1,"instanceName":"1"})]}),makeQuery(id+"F30.opExtrude","SWEPT_FACE",FACE,{"disambiguationData":[OSD([subQ0,sQuery(id+"F0.wireOp",EDGE,"E0.right")])]})]}),makeQuery(id+"F35.opExtrude","SWEPT_FACE",FACE,{"disambiguationData":[OSD([sQuery(id+"F34.wireOp",EDGE,"E55.top")])]})]});}
            extrude(context, id + "F36", {"entities" : qUnion([Q0]), "operationType" : NewBodyOperationType.REMOVE, "oppositeDirection" : true, "depth" : 1 * mm});
        }
        {
            var Q0;
            Q0=makeQuery(id+"F31.opExtrude","CAP_FACE",FACE,{"disambiguationData":[OSD([sQuery(id+"F28.wireOp",EDGE,"E53.right")])],"isStart":false});
            extrude(context, id + "F37", {"entities" : qUnion([Q0]), "operationType" : NewBodyOperationType.ADD, "depth" : .4 * mm});
        }
        {
            var Q0;
            Q0=makeQuery(id+"F29.opExtrude","SWEPT_FACE",FACE,{"disambiguationData":[OSD([sQuery(id+"F28.wireOp",EDGE,"E52.right")])]});
            extrude(context, id + "F38", {"entities" : qUnion([Q0]), "operationType" : NewBodyOperationType.ADD, "depth" : .4 * mm});
        }
        {
            var Q0;
            Q0=makeQuery(id+"F35.opExtrude","CAP_FACE",FACE,{"disambiguationData":[OSD([sQuery(id+"F34.wireOp",EDGE,"E55.bottom"),sQuery(id+"F34.wireOp",EDGE,"E55.top"),sQuery(id+"F34.wireOp",EDGE,"E55.left"),sQuery(id+"F34.wireOp",EDGE,"E55.right"),sQuery(id+"F34.wireOp",EDGE,"E56.bottom"),sQuery(id+"F34.wireOp",EDGE,"E56.top"),sQuery(id+"F34.wireOp",EDGE,"E56.left"),sQuery(id+"F34.wireOp",EDGE,"E56.right")])],"isStart":false});
            var sketch = newSketch(context, id + "F39", { "sketchPlane" : qUnion([Q0])});
            skLineSegment(sketch, "E57.bottom", {"start": v(30.48, -44.7) * mm, "end": v(-30.86, -44.7) * mm});
            skLineSegment(sketch, "E57.top", {"start": v(30.48, 44.72) * mm, "end": v(-30.86, 44.72) * mm});
            skLineSegment(sketch, "E57.left", {"start": v(30.48, -44.7) * mm, "end": v(30.48, 44.72) * mm});
            skLineSegment(sketch, "E57.right", {"start": v(-30.86, -44.7) * mm, "end": v(-30.86, 44.72) * mm});
            skSolve(sketch);
        }
        {
            var Q0;
            Q0 = qSketchRegion(id + "F39", true);
            extrude(context, id + "F40", {"entities" : qUnion([Q0]), "operationType" : NewBodyOperationType.ADD, "depth" : 1.5 * mm});
        }
        {
            var Q0;
            {var subQ0=sQuery(id+"F0.wireOp",EDGE,"E1.right");Q0=makeQuery(id+"F33.boolean.opBoolean","INTERSECT",EDGE,{"derivedFrom":[makeQuery(id+"F9.boolean.opBoolean","SPLIT",FACE,{"disambiguationData":[TD([makeQuery(id+"F9.opExtrude","SWEPT_FACE",FACE,{"disambiguationData":[OSD([sQuery(id+"F8.wireOp",EDGE,"E24.right")])]})])],"derivedFrom":makeQuery(id+"F1.opExtrude","SWEPT_FACE",FACE,{"disambiguationData":[OSD([subQ0])]})}),makeQuery(id+"F33.opExtrude","CAP_FACE",FACE,{"disambiguationData":[OSD([sQuery(id+"F32.wireOp",EDGE,"E54.bottom"),sQuery(id+"F32.wireOp",EDGE,"E54.top"),sQuery(id+"F32.wireOp",EDGE,"E54.left"),sQuery(id+"F32.wireOp",EDGE,"E54.right")])],"isStart":false})]});}
            var Q1;
            {var subQ0=sQuery(id+"F0.wireOp",EDGE,"E1.right");Q1=makeQuery(id+"F33.boolean.opBoolean","INTERSECT",EDGE,{"derivedFrom":[makeQuery(id+"F12.opPattern","COPY",FACE,{"derivedFrom":makeQuery(id+"F9.boolean.opBoolean","SPLIT",FACE,{"disambiguationData":[TD([makeQuery(id+"F9.opExtrude","SWEPT_FACE",FACE,{"disambiguationData":[OSD([sQuery(id+"F8.wireOp",EDGE,"E24.right")])]})])],"derivedFrom":makeQuery(id+"F1.opExtrude","SWEPT_FACE",FACE,{"disambiguationData":[OSD([subQ0])]})}),"instanceName":"1"}),makeQuery(id+"F33.opExtrude","CAP_FACE",FACE,{"disambiguationData":[OSD([sQuery(id+"F32.wireOp",EDGE,"E54.bottom"),sQuery(id+"F32.wireOp",EDGE,"E54.top"),sQuery(id+"F32.wireOp",EDGE,"E54.left"),sQuery(id+"F32.wireOp",EDGE,"E54.right")])],"isStart":false})]});}
            chamfer(context, id + "F41", {"entities" : qUnion([Q0, Q1]), "width" : 5 * mm, "tangentPropagation" : true});
        }
    });
